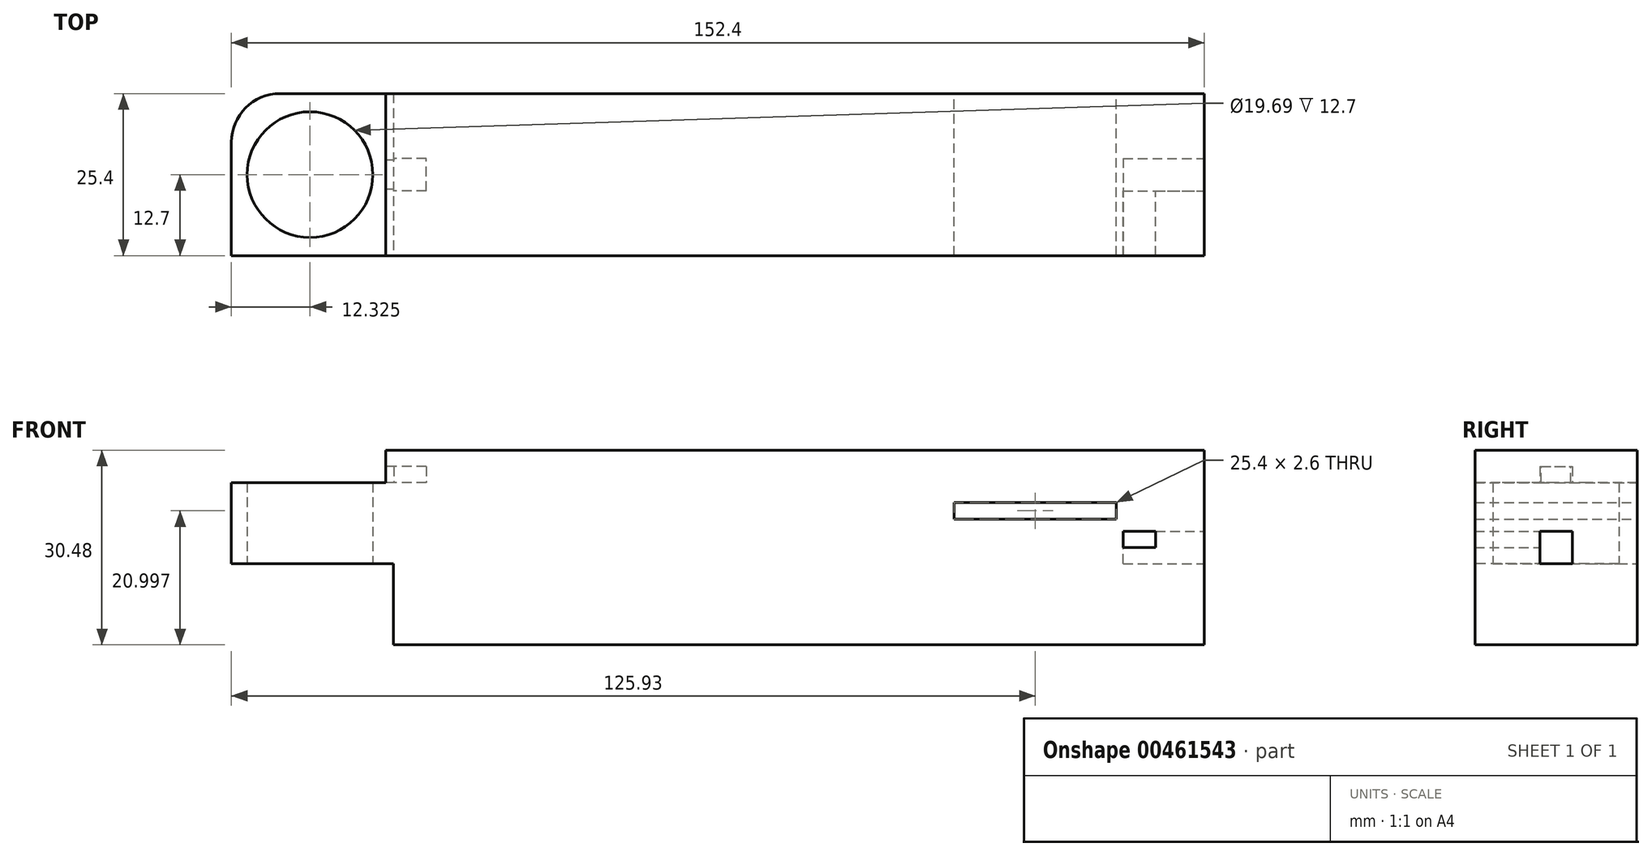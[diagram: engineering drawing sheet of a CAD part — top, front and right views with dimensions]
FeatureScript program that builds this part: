
annotation { "Feature Type Name" : "Feature", "Feature Type Description" : "" }
export const myFeature = defineFeature(function(context is Context, id is Id, definition is map)
    precondition{}
    {
        {
            var Q0;
            Q0=qCreatedBy(makeId("Top.planeOp"),FACE);
            var sketch = newSketch(context, id + "F0", { "sketchPlane" : qUnion([Q0])});
            skLineSegment(sketch, "E0.bottom", {"start": v(-76.2, 76.2) * mm, "end": v(76.2, 76.2) * mm});
            skLineSegment(sketch, "E0.top", {"start": v(-76.2, -76.2) * mm, "end": v(76.2, -76.2) * mm});
            skLineSegment(sketch, "E0.left", {"start": v(-76.2, 76.2) * mm, "end": v(-76.2, -76.2) * mm});
            skLineSegment(sketch, "E0.right", {"start": v(76.2, 76.2) * mm, "end": v(76.2, -76.2) * mm});
            skPoint(sketch, "E0.middle", {"position": v(0, 0) * mm});
            skSolve(sketch);
        }
        {
            var Q0;
            Q0=makeQuery(id+"F0.imprint","IMPRINT",FACE,{"disambiguationData":[TD([[makeQuery(id+"F0.imprint","IMPRINT",EDGE,{"derivedFrom":sQuery(id+"F0.wireOp",EDGE,"E0.bottom")}),-1.0]])]});
            var sketch = newSketch(context, id + "F1", { "sketchPlane" : qUnion([Q0])});
            skLineSegment(sketch, "E1.bottom", {"start": v(-76.2, 12.7) * mm, "end": v(76.2, 12.7) * mm});
            skLineSegment(sketch, "E1.top", {"start": v(-76.2, -12.7) * mm, "end": v(76.2, -12.7) * mm});
            skLineSegment(sketch, "E1.left", {"start": v(-76.2, 12.7) * mm, "end": v(-76.2, -12.7) * mm});
            skLineSegment(sketch, "E1.right", {"start": v(76.2, 12.7) * mm, "end": v(76.2, -12.7) * mm});
            skPoint(sketch, "E1.middle", {"position": v(0, 0) * mm});
            skSolve(sketch);
        }
        {
            var Q0;
            Q0=makeQuery(id+"F1.imprint","IMPRINT",FACE,{"disambiguationData":[TD([[makeQuery(id+"F1.imprint","IMPRINT",EDGE,{"derivedFrom":sQuery(id+"F1.wireOp",EDGE,"E1.bottom")}),-1.0]])]});
            extrude(context, id + "F2", {"entities" : qUnion([Q0]), "depth" : 25.4 * mm});
        }
        {
            var Q0;
            Q0=makeQuery(id+"F0.imprint","IMPRINT",FACE,{"disambiguationData":[TD([[makeQuery(id+"F0.imprint","IMPRINT",EDGE,{"derivedFrom":sQuery(id+"F0.wireOp",EDGE,"E0.bottom")}),-1.0]])]});
            var sketch = newSketch(context, id + "F3", { "sketchPlane" : qUnion([Q0])});
            skCircle(sketch, "E2", {"center": v(-63.88, 0) * mm, "radius": 9.85 * mm});
            skSolve(sketch);
        }
        {
            var Q0;
            Q0=makeQuery(id+"F3.imprint","IMPRINT",FACE,{"disambiguationData":[TD([[makeQuery(id+"F3.imprint","IMPRINT",EDGE,{"derivedFrom":sQuery(id+"F3.wireOp",EDGE,"E2")}),1.0]])]});
            extrude(context, id + "F4", {"entities" : qUnion([Q0]), "operationType" : NewBodyOperationType.REMOVE, "endBound" : BoundingType.THROUGH_ALL, "depth" : 25.4 * mm});
        }
        {
            var Q0;
            Q0=makeQuery(id+"F2.opExtrude","SWEPT_FACE",FACE,{"disambiguationData":[OSD([sQuery(id+"F1.wireOp",EDGE,"E1.left")])]});
            var sketch = newSketch(context, id + "F5", { "sketchPlane" : qUnion([Q0])});
            skLineSegment(sketch, "E3.bottom", {"start": v(-12.7, 0) * mm, "end": v(12.7, 0) * mm});
            skLineSegment(sketch, "E3.top", {"start": v(-12.7, 12.7) * mm, "end": v(12.7, 12.7) * mm});
            skLineSegment(sketch, "E3.left", {"start": v(-12.7, 0) * mm, "end": v(-12.7, 12.7) * mm});
            skLineSegment(sketch, "E3.right", {"start": v(12.7, 0) * mm, "end": v(12.7, 12.7) * mm});
            skSolve(sketch);
        }
        {
            var Q0;
            Q0=makeQuery(id+"F5.imprint","IMPRINT",FACE,{"disambiguationData":[TD([[makeQuery(id+"F5.imprint","IMPRINT",EDGE,{"derivedFrom":sQuery(id+"F5.wireOp",EDGE,"E3.bottom")}),1.0]])]});
            extrude(context, id + "F6", {"entities" : qUnion([Q0]), "operationType" : NewBodyOperationType.REMOVE, "oppositeDirection" : true, "depth" : 25.4 * mm});
        }
        {
            var Q0;
            Q0=makeQuery(id+"F2.opExtrude","SWEPT_FACE",FACE,{"disambiguationData":[OSD([sQuery(id+"F1.wireOp",EDGE,"E1.bottom")])]});
            var sketch = newSketch(context, id + "F7", { "sketchPlane" : qUnion([Q0])});
            skLineSegment(sketch, "E4.bottom", {"start": v(-37.03, 19.7) * mm, "end": v(-62.43, 19.7) * mm});
            skLineSegment(sketch, "E4.top", {"start": v(-37.03, 22.3) * mm, "end": v(-62.43, 22.3) * mm});
            skLineSegment(sketch, "E4.left", {"start": v(-37.03, 19.7) * mm, "end": v(-37.03, 22.3) * mm});
            skLineSegment(sketch, "E4.right", {"start": v(-62.43, 19.7) * mm, "end": v(-62.43, 22.3) * mm});
            skPoint(sketch, "E4.middle", {"position": v(-49.73, 21) * mm});
            skSolve(sketch);
        }
        {
            var Q0;
            Q0=makeQuery(id+"F7.imprint","IMPRINT",FACE,{"disambiguationData":[TD([[makeQuery(id+"F7.imprint","IMPRINT",EDGE,{"derivedFrom":sQuery(id+"F7.wireOp",EDGE,"E4.bottom")}),-1.0]])]});
            extrude(context, id + "F8", {"entities" : qUnion([Q0]), "operationType" : NewBodyOperationType.REMOVE, "oppositeDirection" : true, "depth" : 53.1 * mm});
        }
        {
            var Q0;
            Q0=makeQuery(id+"F2.opExtrude","CAP_FACE",FACE,{"disambiguationData":[OSD([sQuery(id+"F1.wireOp",EDGE,"E1.bottom"),sQuery(id+"F1.wireOp",EDGE,"E1.top"),sQuery(id+"F1.wireOp",EDGE,"E1.left"),sQuery(id+"F1.wireOp",EDGE,"E1.right")])],"isStart":false});
            var sketch = newSketch(context, id + "F9", { "sketchPlane" : qUnion([Q0])});
            skLineSegment(sketch, "E5", {"start": v(-52.03, -12.7) * mm, "end": v(-52.03, 12.7) * mm});
            skSolve(sketch);
        }
        {
            var Q0;
            {var subQ0=sQuery(id+"F9.wireOp",EDGE,"E5");Q0=makeQuery(id+"F9.imprint","IMPRINT",FACE,{"disambiguationData":[TD([[makeQuery(id+"F9.imprint","IMPRINT",EDGE,{"derivedFrom":subQ0}),-1.0]])]});}
            extrude(context, id + "F10", {"entities" : qUnion([Q0]), "operationType" : NewBodyOperationType.ADD, "depth" : 5.08 * mm});
        }
        {
            var Q0;
            Q0=makeQuery(id+"F2.opExtrude","SWEPT_EDGE",EDGE,{"disambiguationData":[OSD([sQuery(id+"F0.wireOp",EDGE,"E0.left"),sQuery(id+"F1.wireOp",EDGE,"E1.bottom"),sQuery(id+"F1.wireOp",EDGE,"E1.left")])]});
            fillet(context, id + "F11", {"entities" : qUnion([Q0]), "radius" : 7.62 * mm, "tangentPropagation" : true, "allowEdgeOverflow" : false});
        }
        {
            var Q0;
            Q0=makeQuery(id+"F10.opExtrude","SWEPT_FACE",FACE,{"disambiguationData":[OSD([sQuery(id+"F9.wireOp",EDGE,"E5")])]});
            var sketch = newSketch(context, id + "F12", { "sketchPlane" : qUnion([Q0])});
            skLineSegment(sketch, "E6.bottom", {"start": v(2.54, 27.94) * mm, "end": v(-2.54, 27.94) * mm});
            skLineSegment(sketch, "E6.top", {"start": v(2.54, 22.86) * mm, "end": v(-2.54, 22.86) * mm});
            skLineSegment(sketch, "E6.left", {"start": v(2.54, 27.94) * mm, "end": v(2.54, 22.86) * mm});
            skLineSegment(sketch, "E6.right", {"start": v(-2.54, 27.94) * mm, "end": v(-2.54, 22.86) * mm});
            skPoint(sketch, "E6.middle", {"position": v(0, 25.4) * mm});
            skSolve(sketch);
        }
        {
            var Q0;
            {var subQ0=sQuery(id+"F12.wireOp",EDGE,"E6.bottom");Q0=makeQuery(id+"F12.imprint","IMPRINT",FACE,{"disambiguationData":[TD([[makeQuery(id+"F12.imprint","IMPRINT",EDGE,{"derivedFrom":subQ0}),1.0]])]});}
            extrude(context, id + "F13", {"entities" : qUnion([Q0]), "operationType" : NewBodyOperationType.REMOVE, "oppositeDirection" : true, "depth" : 6.36 * mm});
        }
        {
            var Q0;
            Q0=makeQuery(id+"F10.opExtrude","SWEPT_FACE",FACE,{"disambiguationData":[OSD([sQuery(id+"F9.wireOp",EDGE,"E5")])]});
            var sketch = newSketch(context, id + "F14", { "sketchPlane" : qUnion([Q0])});
            skLineSegment(sketch, "E7.bottom", {"start": v(-2.54, 25.4) * mm, "end": v(-2.3, 25.4) * mm});
            skLineSegment(sketch, "E7.top", {"start": v(-2.54, 27.94) * mm, "end": v(-2.3, 27.94) * mm});
            skLineSegment(sketch, "E7.left", {"start": v(-2.54, 25.4) * mm, "end": v(-2.54, 27.94) * mm});
            skLineSegment(sketch, "E7.right", {"start": v(-2.3, 25.4) * mm, "end": v(-2.3, 27.94) * mm});
            skLineSegment(sketch, "E8.bottom", {"start": v(2.54, 25.4) * mm, "end": v(2.3, 25.4) * mm});
            skLineSegment(sketch, "E8.top", {"start": v(2.54, 27.94) * mm, "end": v(2.3, 27.94) * mm});
            skLineSegment(sketch, "E8.left", {"start": v(2.54, 25.4) * mm, "end": v(2.54, 27.94) * mm});
            skLineSegment(sketch, "E8.right", {"start": v(2.3, 25.4) * mm, "end": v(2.3, 27.94) * mm});
            skSolve(sketch);
        }
        {
            var Q0;
            Q0=makeQuery(id+"F14.imprint","IMPRINT",FACE,{"disambiguationData":[TD([[makeQuery(id+"F14.imprint","IMPRINT",EDGE,{"derivedFrom":sQuery(id+"F14.wireOp",EDGE,"E7.bottom")}),1.0]])]});
            extrude(context, id + "F15", {"entities" : qUnion([Q0]), "operationType" : NewBodyOperationType.ADD, "oppositeDirection" : true, "depth" : 1.27 * mm});
        }
        {
            var Q0;
            Q0=makeQuery(id+"F14.imprint","IMPRINT",FACE,{"disambiguationData":[TD([[makeQuery(id+"F14.imprint","IMPRINT",EDGE,{"derivedFrom":sQuery(id+"F14.wireOp",EDGE,"E8.bottom")}),-1.0]])]});
            extrude(context, id + "F16", {"entities" : qUnion([Q0]), "operationType" : NewBodyOperationType.ADD, "oppositeDirection" : true, "depth" : 1.27 * mm});
        }
        {
            var Q0;
            {var subQ0=sQuery(id+"F1.wireOp",EDGE,"E1.right");Q0=makeQuery(id+"F10.boolean.opBoolean","MERGE",FACE,{"derivedFrom":[makeQuery(id+"F2.opExtrude","SWEPT_FACE",FACE,{"disambiguationData":[OSD([subQ0])]}),makeQuery(id+"F10.opExtrude","SWEPT_FACE",FACE,{"disambiguationData":[OSD([subQ0])]})]});}
            var sketch = newSketch(context, id + "F17", { "sketchPlane" : qUnion([Q0])});
            skLineSegment(sketch, "E9.bottom", {"start": v(2.54, 12.7) * mm, "end": v(-2.54, 12.7) * mm});
            skLineSegment(sketch, "E9.top", {"start": v(2.54, 17.78) * mm, "end": v(-2.54, 17.78) * mm});
            skLineSegment(sketch, "E9.left", {"start": v(2.54, 12.7) * mm, "end": v(2.54, 17.78) * mm});
            skLineSegment(sketch, "E9.right", {"start": v(-2.54, 12.7) * mm, "end": v(-2.54, 17.78) * mm});
            skPoint(sketch, "E9.middle", {"position": v(0, 15.24) * mm});
            skPoint(sketch, "E9.middle.positionSnap0", {"position": v(0, 0) * mm});
            skPoint(sketch, "E9.middle.positionSnap1", {"position": v(-12.7, 15.24) * mm});
            skPoint(sketch, "E9.centerSnap0", {"position": v(0, 0) * mm});
            skPoint(sketch, "E9.centerSnap1", {"position": v(-12.7, 15.24) * mm});
            skSolve(sketch);
        }
        {
            var Q0;
            Q0=makeQuery(id+"F17.imprint","IMPRINT",FACE,{"disambiguationData":[TD([[makeQuery(id+"F17.imprint","IMPRINT",EDGE,{"derivedFrom":sQuery(id+"F17.wireOp",EDGE,"E9.bottom")}),-1.0]])]});
            extrude(context, id + "F18", {"entities" : qUnion([Q0]), "operationType" : NewBodyOperationType.REMOVE, "oppositeDirection" : true, "depth" : 12.7 * mm});
        }
        {
            var Q0;
            Q0=makeQuery(id+"F18.boolean.opBoolean","COPY",FACE,{"derivedFrom":makeQuery(id+"F18.opExtrude","SWEPT_FACE",FACE,{"disambiguationData":[OSD([sQuery(id+"F17.wireOp",EDGE,"E9.right")])]})});
            var sketch = newSketch(context, id + "F19", { "sketchPlane" : qUnion([Q0])});
            skLineSegment(sketch, "E10.bottom", {"start": v(-63.5, 17.78) * mm, "end": v(-68.58, 17.78) * mm});
            skLineSegment(sketch, "E10.top", {"start": v(-63.5, 15.24) * mm, "end": v(-68.58, 15.24) * mm});
            skLineSegment(sketch, "E10.left", {"start": v(-63.5, 17.78) * mm, "end": v(-63.5, 15.24) * mm});
            skLineSegment(sketch, "E10.right", {"start": v(-68.58, 17.78) * mm, "end": v(-68.58, 15.24) * mm});
            skSolve(sketch);
        }
        {
            var Q0;
            Q0 = qSketchRegion(id + "F19", true);
            extrude(context, id + "F20", {"entities" : qUnion([Q0]), "operationType" : NewBodyOperationType.REMOVE, "oppositeDirection" : true, "depth" : 25.4 * mm});
        }
    });
